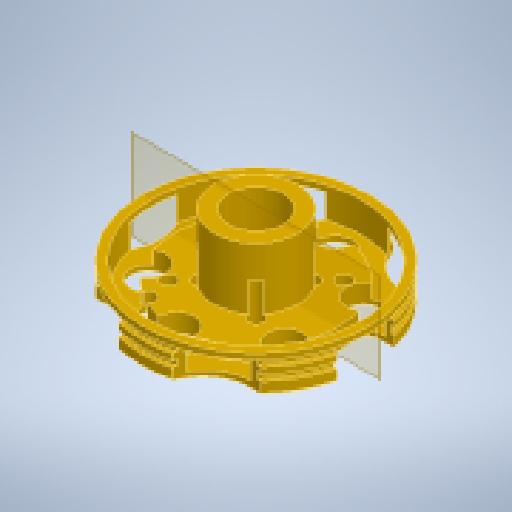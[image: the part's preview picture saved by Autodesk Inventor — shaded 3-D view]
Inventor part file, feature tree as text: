
AUTODESK INVENTOR PART (.ipt)
format: ipt  version: 2023.1 (Build 271208000, 208)  size: 433,664 bytes
history: native  units: in
note: dims shown in document units (in); Inventor stores cm internally (conversion verified against a paired STEP export)
features: sketch x2, chamfer x2, extrude x2, revolve x1
ambient origin geometry x8: Origin, YZ Plane, XZ Plane, XY Plane, X Axis, Y Axis, Z Axis, Center Point
bodies: Solid1 (feature_tree)
feature tree (7):
  revolve  "Revolution1"  [1 undecoded]
  sketch  "Sketch2"  dims[d2=0.0531in d3=0.0689in d4=0.0591in d5=0.0492in d6=0.0492in d7=0.7874in d9=0.0984in d10=0.3937in d12=0.3937in d14=0.6496in d15=0.1575in d16=0.2165in d17=0.6496in d18=0.3346in d19=90.0deg d20=1.2598in d21=0.2756in d22=30.0deg d23=1.5354in d24=0.7874in d25=0.6299in d26=0.748in d27=0.9843in d28=45.0deg d30=0.1181in d31=0.1181in d32=0.1181in d33=0.7874in d35=360.0deg d37=2.3622in d39=360.0deg d41=1.2402in d42=30.0deg d43=0.1181in d44=1.1811in d46=360.0deg d48=0.0197in d49=0.0787in d50=45.0deg d51=0.2461in d52=0.0in d53=0.3937in d54=0.0in d55=0.0098in d56=0.0787in d57=45.0deg d58=0.4626in d59=1.3386in d60=0.1575in]
  chamfer  "Chamfer1"  Distance=0.0689in
  extrude  "Extrusion1"  Depth=0.3937in
  extrude  "Extrusion2"  Depth=0.3937in
  chamfer  "Chamfer2"  Distance=0.0492in
  sketch  "Sketch1"  dims[d0=0.9055in d1=0.2953in]
note: 1 required parameter value undecoded (feature->parameter linkage not recoverable at this tier; creation-order binding heuristic only, values carry confidence <= 0.55)
